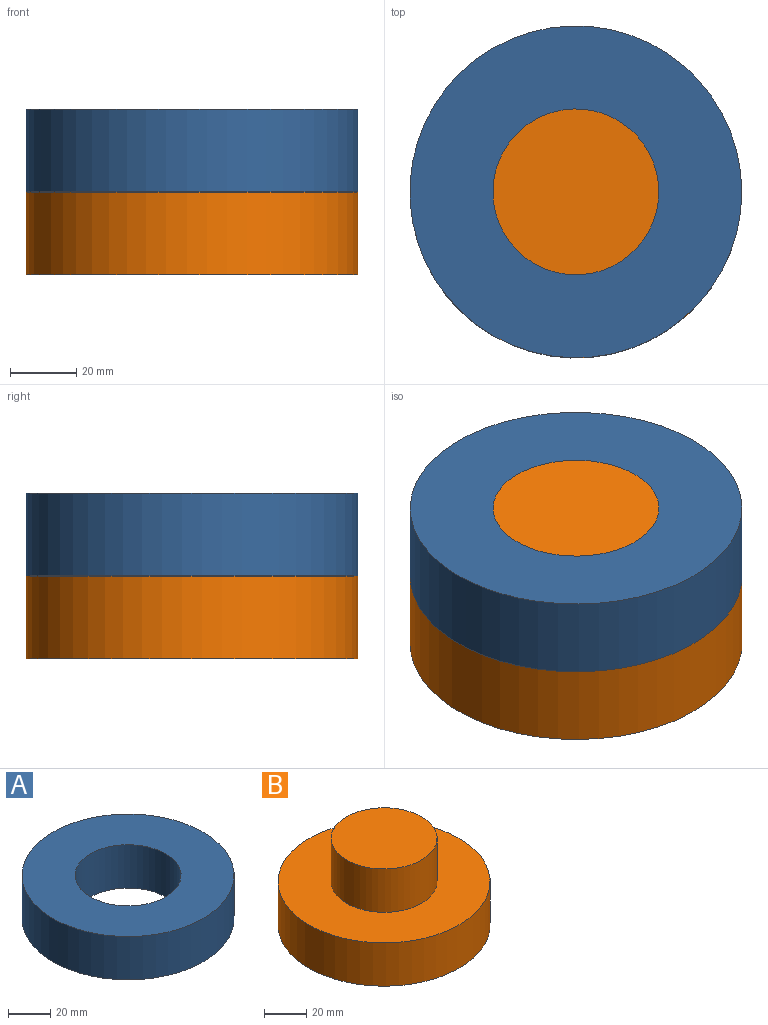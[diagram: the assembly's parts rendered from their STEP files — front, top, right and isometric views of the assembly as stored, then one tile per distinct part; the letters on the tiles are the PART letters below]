
ASSEMBLY  parts=2 mates=1
PART A: 4 faces, bbox 100x100x25 mm
  f0: cylinder r=50mm len=100mm, axis (0,0,-1), area 7854mm2, adj f1,f2
  f1: plane 100x100mm, normal (0,0,1), area 5890.5mm2, adj f0,f3
  f2: plane 100x100mm, normal (0,0,-1), area 5890.5mm2, adj f0,f3
  f3: cylinder r=25mm len=50mm, axis (0,0,1), area 3927mm2, adj f1,f2
PART B: 5 faces, bbox 100x100x50 mm
  f0: cylinder r=50mm len=100mm, axis (0,0,-1), area 7854mm2, adj f1,f2
  f1: plane 100x100mm, normal (0,0,1), area 5890.5mm2, adj f0,f3
  f2: plane 100x100mm, normal (0,0,-1), area 7854mm2, adj f0
  f3: cylinder r=25mm len=50mm, axis (0,0,-1), area 3927mm2, adj f1,f4
  f4: plane 50x50mm, normal (0,0,1), area 1963.5mm2, adj f3
PLACE A t=(-85.2,128.84,57.94)mm
PLACE B t=(-85.2,128.84,32.94)mm
MATE fastened B.f0 <-> A.f0  axis (0,0,1) through (-85.2,128.84,57.94)mm
